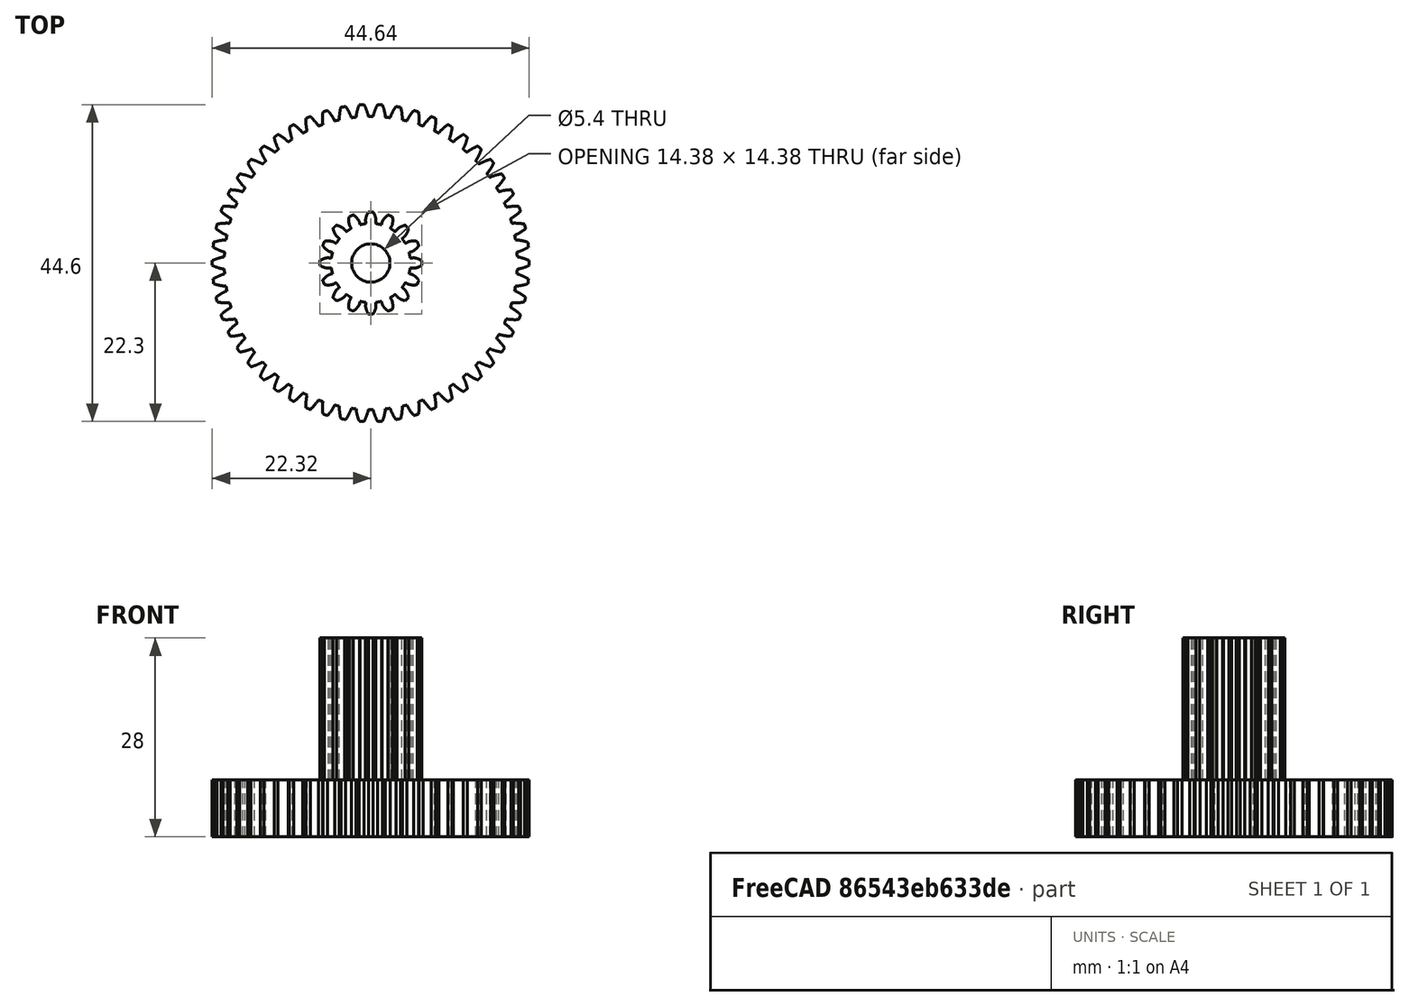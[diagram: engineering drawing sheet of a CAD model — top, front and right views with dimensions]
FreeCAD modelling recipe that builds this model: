
FCSTD DOCUMENT  (FreeCAD 0.18R16110 (Git))
Label: Gear
License: All rights reserved
LicenseURL: http://en.wikipedia.org/wiki/All_rights_reserved
objects: Part::FeaturePython×2, Part::MultiFuse×1, Part::Cylinder×1, Spreadsheet::Sheet×1, Part::Cut×1, Mesh::Feature×1
note: 5 computed .brp shape members not serialized (recipe doc carries the construction recipe); baked Part::Feature solids carry a one-line shape summary decoded from their .brp

FEATURE [Part::FeaturePython] InvoluteGear003  # WARN: FeaturePython — macro-defined, semantics opaque (R4)
  backlash = 0
  beta = 0
  clearance = 0.2
  double_helix = false
  head = -0.2
  height = 28
  module = 0.8
  numpoints = 10
  pressure_angle = 20
  reversed_backlash = false
  shift = 0.2
  simple = false
  teeth = 16
  undercut = false
  expr: height = Spreadsheet.z1_height
  expr: teeth = Spreadsheet.z1_teeth
  expr: shift = Spreadsheet.z1_shift
  expr: module = Spreadsheet.modul
FEATURE [Part::FeaturePython] InvoluteGear004  # WARN: FeaturePython — macro-defined, semantics opaque (R4)
  backlash = 0
  beta = 0
  clearance = 0.2
  double_helix = false
  head = -0.1
  height = 8
  module = 0.8
  numpoints = 10
  pressure_angle = 20
  reversed_backlash = false
  shift = 0
  simple = false
  teeth = 54
  undercut = false
FEATURE [Part::MultiFuse] Fusion
  Shapes = -> [InvoluteGear003,InvoluteGear004]
FEATURE [Part::Cylinder] Cylinder001  label="Zylinder001"
  Angle = 360
  AttacherType = Attacher::AttachEngine3D
  Height = 28
  Radius = 2.7
  expr: Height = Spreadsheet.z1_height
  expr: Radius = Spreadsheet.z1_daxis + Spreadsheet.tolerance
FEATURE [Spreadsheet::Sheet] Spreadsheet
  cells = A1=Modul; B1(modul)=0.8; D1=tolerance; E1(tolerance)=0.2; G1=tolerance gear; H1(tolerance_gear)=0; A3=Zahnstange; D3=Zahnrad_1; G3=Zahnrad_2; J3=Ritzel; M3=Stepper; P3=Casing; A4=ra; B4(z_ra)=11; D4=#teeth; E4(z1_teeth)=16; G4=#teeth; H4(z2_teeth)=54; J4=#teeth; K4(ritzel_teeth)=16; M4=axis d; N4(stepper_daxis)=5; P4=gear casing sgear; Q4(casing_sgear)=2; A5=di; B5(z_ri)=8; D5=shift; E5(z1_shift)=0.2; G5=shift; H5(z2_shift)=0; J5=shift; K5(ritzel_shift)=0.3; M5=shaft l; N5(stepper_lshaft)=18; P5=rack casing srack; Q5(casing_srack)=2; A6=l; B6(z_l)==casing_ymax - casing_ymin + casing_scase; D6=pitch d; E6(z1_dpi)==modul * z1_teeth; G6=pitch d; H6(z2_dpi)==modul * z2_teeth; J6=pitch d; K6(ritzel_dpi)==modul * ritzel_teeth; M6=outside  sa; N6(stepper_sa)=28; P6=casing scase; Q6(casing_scase)=5; D7=outside d; E7(z1_da)==z1_dpi + 2 * (1 + z1_shift) * modul; G7=outside d; H7(z2_da)==z2_dpi + 2 * (1 + z2_shift) * modul; J7=outside d; K7(ritzel_da)==ritzel_dpi + 2 * (1 + ritzel_shift) * modul; M7=mount screw s; N7(stepper_sscrew)=23; P7=casing ssup; Q7(casing_ssup)=5; A8=rack height; B8(z_h)==z_th; D8=center distance; E8(z1_dc)==z1_dpi / 2 + z1_shift * modul + tolerance_gear; G8=center distance; H8(z2_dc)==z2_dpi / 2 + z2_shift * modul + tolerance_gear; J8=center distace; K8(ritzel_dc)==ritzel_dpi / 2 + ritzel_shift * modul + tolerance_gear; M8=mount d; N8(stepper_dmount)=22; P8=überlappung sjoin; Q8(casing_sjoin)=0.9; A9=rack thickness; B9(z_th)==2 * z_ra + 2; M9=mount heigth; N9(stepper_hmount)=2; A10=rack teeth width; B10(z_w)=8; D10=y Shift; E10(z1_yshift)=8; G10=height; H10(z2_h)=8; J10=angle z1; K10(ritzel_angle)=-65; M10=mount dscrew; N10(stepper_dscrew)=2.5; P10=casing y_min; Q10(casing_ymin)==-(Spreadsheet.z2_da / 2 + Spreadsheet.casing_scase + Spreadsheet.casing_sgear - Spreadsheet.z1_yshift - casing_sjoin + Spreadsheet.tolerance) * 0 + Spreadsheet.ritzel_ypos - stepper_sa / 2 - casing_scase; A11=#teeth; B11(z_teeth)=45; D11=height; E11(z1_height)==Spreadsheet.z_w * 3 / 4 + Spreadsheet.z2_dr + Spreadsheet.z2_h + Spreadsheet.z_ra; G11=distance rack; H11(z2_dr)=3; P11=casing x_min; Q11(casing_xmin)==-(Spreadsheet.z_ra * cos(asin(Spreadsheet.z_w / 2 / Spreadsheet.z_ra)) - Spreadsheet.modul + Spreadsheet.z_ra + Spreadsheet.casing_srack + Spreadsheet.casing_scase - Spreadsheet.casing_sjoin); D12=axis r; E12(z1_daxis)=2.5; G12=axis r; J12=x_pos; K12(ritzel_xpos)==Spreadsheet.z1_dc + cos(Spreadsheet.ritzel_angle) * (Spreadsheet.z2_dc + Spreadsheet.ritzel_dc); P12=casing z_min; Q12(casing_zmin)==-(Spreadsheet.z2_dr + Spreadsheet.z2_h - (Spreadsheet.z_h / 2 - Spreadsheet.z_ra) + Spreadsheet.tolerance) * 0 - 20.5; J13=y_pos; K13(ritzel_ypos)==Spreadsheet.z1_yshift + sin(Spreadsheet.ritzel_angle) * (Spreadsheet.z2_dc + Spreadsheet.ritzel_dc); G14=z_pos; H14(z2_zpos)==-(Spreadsheet.z2_dr + Spreadsheet.z2_h - (Spreadsheet.z_h / 2 - Spreadsheet.z_ra)); P14=casing z_max; Q14(casing_zmax)==(2 * Spreadsheet.casing_srack + Spreadsheet.z_th - Spreadsheet.casing_sjoin) * 0 + 44.5; G15=winkel 1; H15(z2_w1)==165°; P15=casing x_max; Q15(casing_xmax)==Spreadsheet.ritzel_xpos + stepper_sa / 2 + casing_scase + 2; A16=65; B16==-A16 / 2; C16==casing_xmax - casing_xmin - tolerance - casing_scase; G16=winkel 2; H16(z2_w2)==45°; P16=casing y_max; Q16(casing_ymax)==(Spreadsheet.ritzel_ypos + stepper_sa / 2 + 2) * 0 + 31; A17=8; B17==B16 + A18; C17==B17 ^ A20 * A19; G17=winkel 3; H17(z2_w3)==-49°; A18==A16 / A17; B18==B17 + A18; C18==B18 ^ A20 * A19; G18=winkel 4; H18(z2_w4)==-138°; A19==C16 / B16 ^ A20; B19==B18 + A18; C19==B19 ^ A20 * A19; A20=4; B20==B19 + A18; C20==B20 ^ A20 * A19; B21==B20 + A18; C21==B21 ^ A20 * A19; B22==B21 + A18; C22==B22 ^ A20 * A19; B23==B22 + A18; C23==B23 ^ A20 * A19; B24==B23 + A18; C24==B24 ^ A20 * A19
FEATURE [Part::Cut] Cut  label="Gear"
  Base = -> Fusion
  Placement = pos=(6.56,8,-10) rot=(0,0,1;0rad)
  Tool = -> Cylinder001
  expr: Placement.Base.x = Spreadsheet.z1_dc + Spreadsheet.tolerance_gear
  expr: Placement.Base.y = Spreadsheet.z1_yshift
  expr: Placement.Base.z = Spreadsheet.z2_zpos
FEATURE [Mesh::Feature] Mesh  label="Gear (Meshed)"
